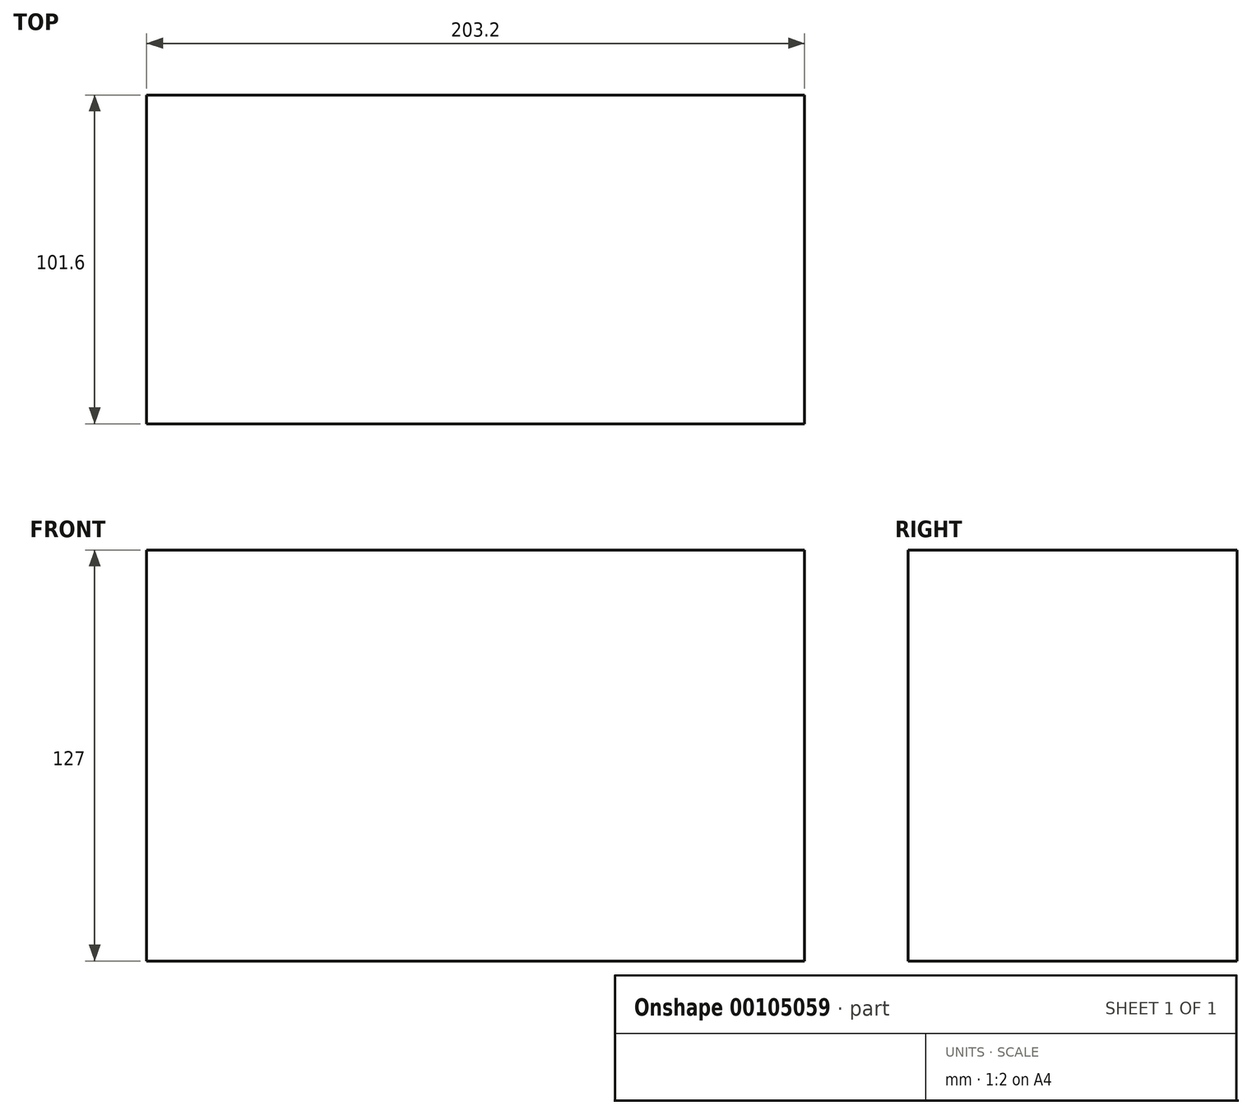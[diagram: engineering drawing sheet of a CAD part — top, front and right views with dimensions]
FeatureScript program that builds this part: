
annotation { "Feature Type Name" : "Feature", "Feature Type Description" : "" }
export const myFeature = defineFeature(function(context is Context, id is Id, definition is map)
    precondition{}
    {
        {
            var Q0;
            Q0=qCreatedBy(makeId("Top.planeOp"),FACE);
            var sketch = newSketch(context, id + "F0", { "sketchPlane" : qUnion([Q0])});
            skLineSegment(sketch, "E0.bottom", {"start": v(-101.27, 50.02) * mm, "end": v(101.93, 50.02) * mm});
            skLineSegment(sketch, "E0.top", {"start": v(-101.27, -51.58) * mm, "end": v(101.93, -51.58) * mm});
            skLineSegment(sketch, "E0.left", {"start": v(-101.27, 50.02) * mm, "end": v(-101.27, 18.27) * mm});
            skLineSegment(sketch, "E0.right", {"start": v(101.93, 50.02) * mm, "end": v(101.93, 18.27) * mm});
            skLineSegment(sketch, "E1", {"start": v(-101.27, 18.27) * mm, "end": v(-63.17, 18.27) * mm});
            skLineSegment(sketch, "E2", {"start": v(-63.17, 18.27) * mm, "end": v(-63.17, -19.83) * mm});
            skLineSegment(sketch, "E3", {"start": v(-63.17, -19.83) * mm, "end": v(-101.27, -19.83) * mm});
            skLineSegment(sketch, "E4", {"start": v(-50.47, 50.02) * mm, "end": v(51.13, 50.02) * mm});
            skLineSegment(sketch, "E5", {"start": v(51.13, 50.02) * mm, "end": v(0.33, -51.58) * mm});
            skLineSegment(sketch, "E6", {"start": v(0.33, -51.58) * mm, "end": v(-50.47, 50.02) * mm});
            skLineSegment(sketch, "E7.trimOffspring", {"start": v(-101.27, -19.83) * mm, "end": v(-101.27, -51.58) * mm});
            skLineSegment(sketch, "E8", {"start": v(101.93, 18.27) * mm, "end": v(63.83, 18.27) * mm});
            skLineSegment(sketch, "E9", {"start": v(63.83, 18.27) * mm, "end": v(63.83, -19.83) * mm});
            skLineSegment(sketch, "E10", {"start": v(63.83, -19.83) * mm, "end": v(101.93, -19.83) * mm});
            skLineSegment(sketch, "E11.trimOffspring", {"start": v(101.93, -19.83) * mm, "end": v(101.93, -51.58) * mm});
            skSolve(sketch);
        }
        {
            var Q0;
            Q0=qCreatedBy(makeId("Front.planeOp"),FACE);
            var sketch = newSketch(context, id + "F1", { "sketchPlane" : qUnion([Q0])});
            skLineSegment(sketch, "E12.bottom", {"start": v(-101.27, 0) * mm, "end": v(101.93, 0) * mm});
            skLineSegment(sketch, "E12.top", {"start": v(-101.27, 127) * mm, "end": v(101.93, 127) * mm});
            skLineSegment(sketch, "E12.left", {"start": v(-101.27, 0) * mm, "end": v(-101.27, 127) * mm});
            skLineSegment(sketch, "E12.right", {"start": v(101.93, 0) * mm, "end": v(101.93, 127) * mm});
            skSolve(sketch);
        }
        {
            var Q0;
            Q0 = qSketchRegion(id + "F1", true);
            extrude(context, id + "F2", {"entities" : qUnion([Q0]), "endBound" : BoundingType.SYMMETRIC, "depth" : 101.6 * mm});
        }
    });
